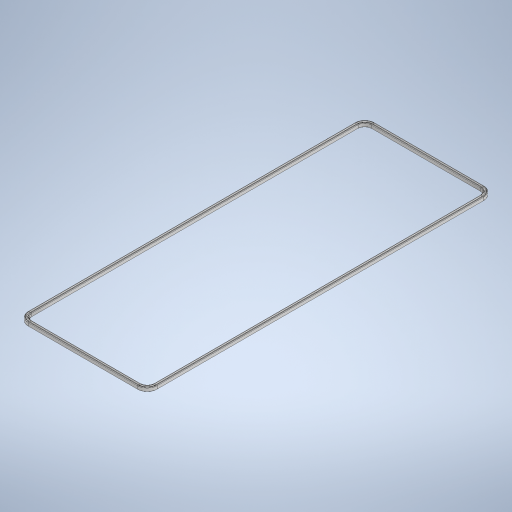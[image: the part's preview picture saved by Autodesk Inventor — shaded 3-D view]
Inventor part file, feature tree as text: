
AUTODESK INVENTOR PART (.ipt)
format: ipt  version: 2023 (Build 270158000, 158)  size: 383,488 bytes
history: native  units: in
note: dims shown in document units (in); Inventor stores cm internally (conversion verified against a paired STEP export)
features: chamfer x3, extrude x2, sketch x2
ambient origin geometry x8: Origin, YZ Plane, XZ Plane, XY Plane, X Axis, Y Axis, Z Axis, Center Point
bodies: Solid1 (feature_tree)
feature tree (7):
  extrude  "Extrusion1"  Depth=0.9449in
  extrude  "Extrusion2"  Depth=6.063in
  chamfer  "Chamfer3"  Distance=0.1575in
  chamfer  "Chamfer4"  Distance=0.1575in
  chamfer  "Chamfer5"  Distance=0.1575in
  sketch  "Sketch1"  dims[d0=0.9449in d1=0.9449in]
  sketch  "Sketch2"  dims[d2=0.9449in d3=0.9449in d6=0.1575in d7=0.1575in d8=0.1575in d9=0.1575in d10=0.1575in d11=0.1575in d12=0.1575in d13=0.1575in d14=0.1772in d15=0.0in d16=0.0984in d17=0.0591in d18=0.0394in d19=0.0in d26=0.0197in d27=0.0394in d28=45.0deg d29=0.0197in d30=0.0394in d31=45.0deg d32=0.0197in d33=0.0394in d34=45.0deg d35=16.2992in d36=6.063in]
